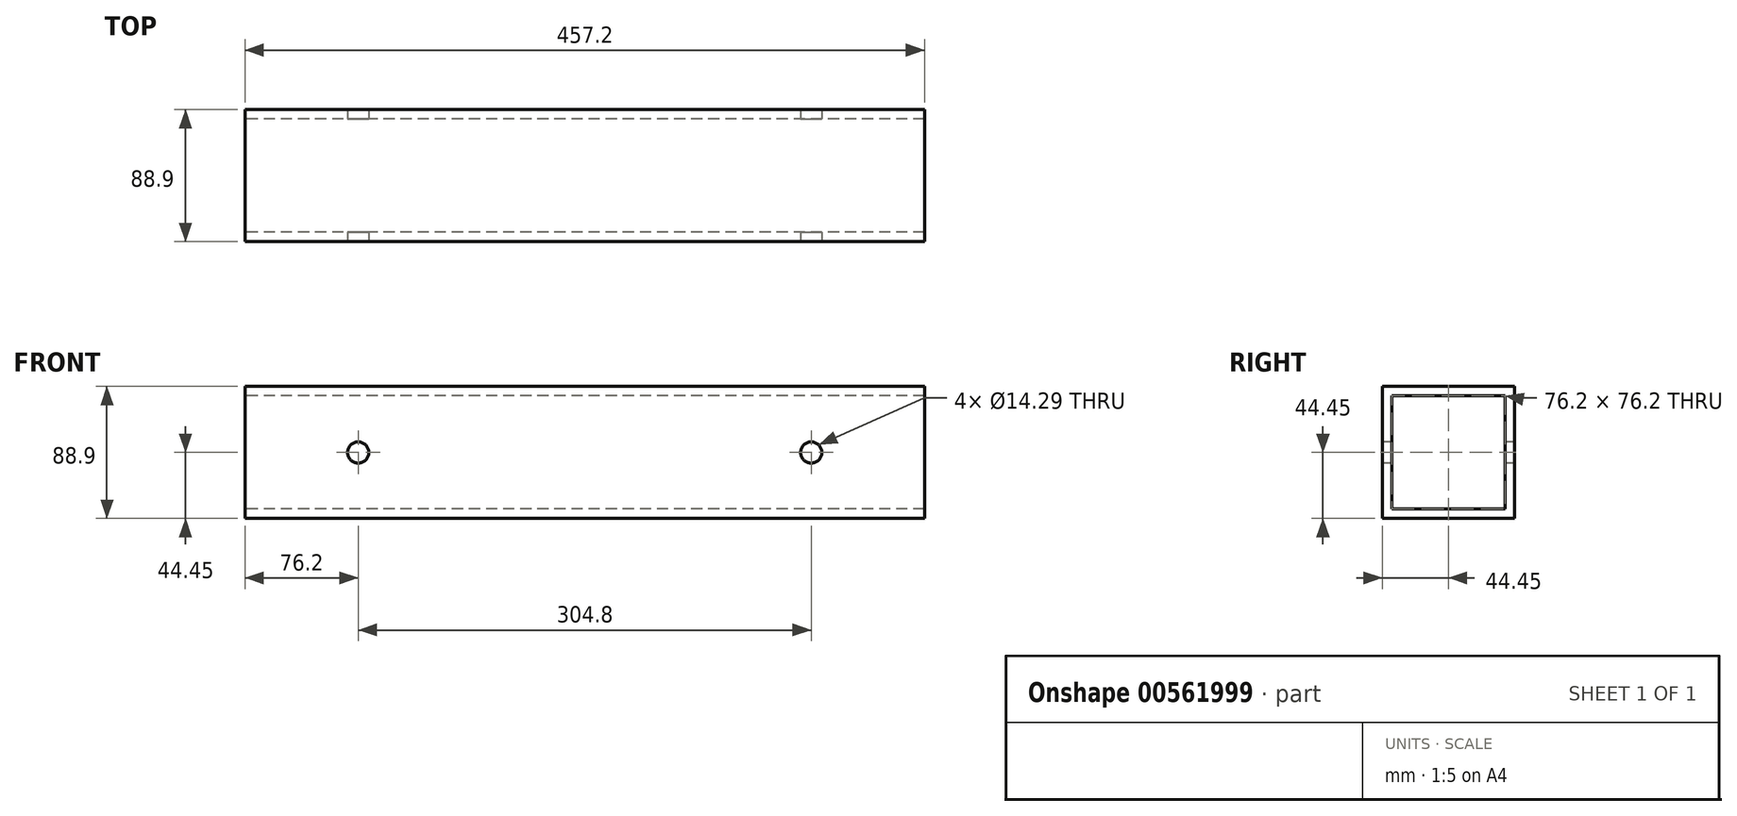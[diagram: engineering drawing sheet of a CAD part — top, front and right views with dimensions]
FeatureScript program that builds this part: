
annotation { "Feature Type Name" : "Feature", "Feature Type Description" : "" }
export const myFeature = defineFeature(function(context is Context, id is Id, definition is map)
    precondition{}
    {
        {
            var Q0;
            Q0=qCreatedBy(makeId("Right.planeOp"),FACE);
            var sketch = newSketch(context, id + "F0", { "sketchPlane" : qUnion([Q0])});
            skLineSegment(sketch, "E0.bottom", {"start": v(44.45, -44.45) * mm, "end": v(-44.45, -44.45) * mm});
            skLineSegment(sketch, "E0.top", {"start": v(44.45, 44.45) * mm, "end": v(-44.45, 44.45) * mm});
            skLineSegment(sketch, "E0.left", {"start": v(44.45, -44.45) * mm, "end": v(44.45, 44.45) * mm});
            skLineSegment(sketch, "E0.right", {"start": v(-44.45, -44.45) * mm, "end": v(-44.45, 44.45) * mm});
            skPoint(sketch, "E0.middle", {"position": v(0, 0) * mm});
            skLineSegment(sketch, "E1.bottom", {"start": v(38.1, -38.1) * mm, "end": v(-38.1, -38.1) * mm});
            skLineSegment(sketch, "E1.top", {"start": v(38.1, 38.1) * mm, "end": v(-38.1, 38.1) * mm});
            skLineSegment(sketch, "E1.left", {"start": v(38.1, -38.1) * mm, "end": v(38.1, 38.1) * mm});
            skLineSegment(sketch, "E1.right", {"start": v(-38.1, -38.1) * mm, "end": v(-38.1, 38.1) * mm});
            skLineSegment(sketch, "E2", {"start": v(0, 0) * mm, "end": v(-44.45, 44.45) * mm, "construction": true});
            skSolve(sketch);
        }
        {
            var Q0;
            Q0 = qSketchRegion(id + "F0", true);
            extrude(context, id + "F1", {"entities" : qUnion([Q0]), "depth" : 457.2 * mm, "offsetDistance" : 25.4 * mm});
        }
        {
            var Q0;
            Q0=makeQuery(id+"F1.opExtrude","SWEPT_FACE",FACE,{"disambiguationData":[OSD([sQuery(id+"F0.wireOp",EDGE,"E0.right")])]});
            var sketch = newSketch(context, id + "F2", { "sketchPlane" : qUnion([Q0])});
            skLineSegment(sketch, "E3", {"start": v(0, 0) * mm, "end": v(457.2, 0) * mm, "construction": true});
            skCircle(sketch, "E4", {"center": v(381, 0) * mm, "radius": 7.14 * mm});
            skLineSegment(sketch, "E5", {"start": v(228.6, 44.45) * mm, "end": v(228.6, -44.45) * mm, "construction": true});
            skCircle(sketch, "E6.MirrorC", {"center": v(76.2, 0) * mm, "radius": 7.14 * mm});
            skSolve(sketch);
        }
        {
            var Q0;
            Q0 = qSketchRegion(id + "F2", true);
            extrude(context, id + "F3", {"entities" : qUnion([Q0]), "operationType" : NewBodyOperationType.REMOVE, "endBound" : BoundingType.THROUGH_ALL, "oppositeDirection" : true, "depth" : 25.4 * mm, "offsetDistance" : 25.4 * mm});
        }
    });
